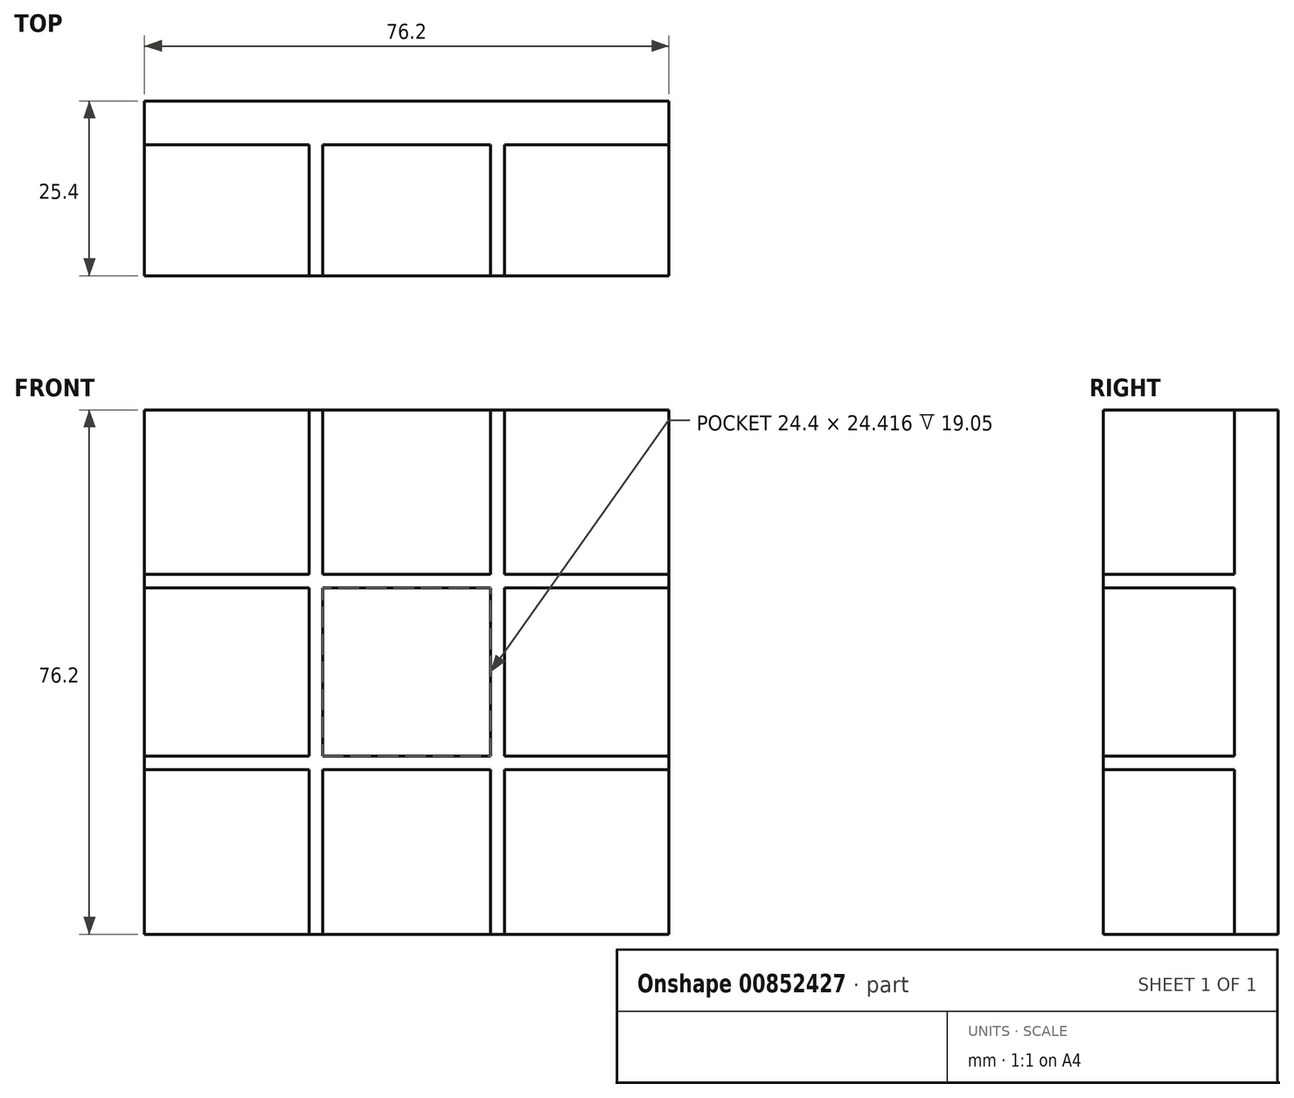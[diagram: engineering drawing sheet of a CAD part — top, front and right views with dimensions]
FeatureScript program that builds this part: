
annotation { "Feature Type Name" : "Feature", "Feature Type Description" : "" }
export const myFeature = defineFeature(function(context is Context, id is Id, definition is map)
    precondition{}
    {
        {
            var Q0;
            Q0=qCreatedBy(makeId("Front.planeOp"),FACE);
            var sketch = newSketch(context, id + "F0", { "sketchPlane" : qUnion([Q0])});
            skLineSegment(sketch, "E0.bottom", {"start": v(-38.2, 49.7) * mm, "end": v(38, 49.7) * mm});
            skLineSegment(sketch, "E0.top", {"start": v(-38.2, -26.5) * mm, "end": v(38, -26.5) * mm});
            skLineSegment(sketch, "E0.left", {"start": v(-38.2, 49.7) * mm, "end": v(-38.2, -26.5) * mm});
            skLineSegment(sketch, "E0.right", {"start": v(38, 49.7) * mm, "end": v(38, -26.5) * mm});
            skSolve(sketch);
        }
        {
            var Q0;
            Q0=makeQuery(id+"F0.imprint","IMPRINT",FACE,{"disambiguationData":[TD([[makeQuery(id+"F0.imprint","IMPRINT",EDGE,{"derivedFrom":sQuery(id+"F0.wireOp",EDGE,"E0.bottom")}),-1.0]])]});
            var sketch = newSketch(context, id + "F1", { "sketchPlane" : qUnion([Q0])});
            skLineSegment(sketch, "E1", {"start": v(-13.3, 49.7) * mm, "end": v(-13.3, -26.5) * mm});
            skLineSegment(sketch, "E2", {"start": v(13.1, 49.7) * mm, "end": v(13.1, -26.5) * mm});
            skLineSegment(sketch, "E3", {"start": v(-38.2, 24.8) * mm, "end": v(38, 24.8) * mm});
            skLineSegment(sketch, "E4", {"start": v(-38.2, -1.62) * mm, "end": v(38, -1.62) * mm});
            skSolve(sketch);
        }
        {
            var Q0;
            Q0=qCreatedBy(makeId("Front.planeOp"),FACE);
            var sketch = newSketch(context, id + "F2", { "sketchPlane" : qUnion([Q0])});
            skLineSegment(sketch, "E5", {"start": v(14.1, 49.7) * mm, "end": v(14.1, -26.5) * mm});
            skLineSegment(sketch, "E6", {"start": v(-14.3, 49.7) * mm, "end": v(-14.3, -26.5) * mm});
            skLineSegment(sketch, "E7", {"start": v(-38.2, 25.8) * mm, "end": v(38, 25.8) * mm});
            skLineSegment(sketch, "E8", {"start": v(-38.2, -2.62) * mm, "end": v(38, -2.62) * mm});
            skLineSegment(sketch, "E9", {"start": v(-38.2, -0.62) * mm, "end": v(38, -0.62) * mm});
            skLineSegment(sketch, "E10", {"start": v(-38.2, 23.8) * mm, "end": v(38, 23.8) * mm});
            skLineSegment(sketch, "E11", {"start": v(-12.3, 49.7) * mm, "end": v(-12.3, -26.5) * mm});
            skLineSegment(sketch, "E12", {"start": v(12.1, 49.7) * mm, "end": v(12.1, -26.5) * mm});
            skSolve(sketch);
        }
        {
            var Q0;
            Q0=makeQuery(id+"F0.imprint","IMPRINT",FACE,{"disambiguationData":[TD([[makeQuery(id+"F0.imprint","IMPRINT",EDGE,{"derivedFrom":sQuery(id+"F0.wireOp",EDGE,"E0.bottom")}),-1.0]])]});
            extrude(context, id + "F3", {"entities" : qUnion([Q0]), "depth" : 6.35 * mm, "offsetDistance" : 25.4 * mm});
        }
        {
            var Q0;
            Q0=sQuery(id+"F2.wireOp",EDGE,"E6");
            extrude(context, id + "F4", {"bodyType" : ToolBodyType.SURFACE, "surfaceEntities" : qUnion([Q0]), "depth" : 25.4 * mm, "offsetDistance" : 25.4 * mm});
        }
        {
            var Q0;
            Q0=sQuery(id+"F2.wireOp",EDGE,"E11");
            var Q1;
            Q1=sQuery(id+"F2.wireOp",EDGE,"E12");
            var Q2;
            Q2=sQuery(id+"F2.wireOp",EDGE,"E5");
            extrude(context, id + "F5", {"bodyType" : ToolBodyType.SURFACE, "surfaceEntities" : qUnion([Q0, Q1, Q2]), "depth" : 25.4 * mm, "offsetDistance" : 25.4 * mm});
        }
        {
            var Q0;
            Q0=sQuery(id+"F2.wireOp",EDGE,"E7");
            var Q1;
            Q1=sQuery(id+"F2.wireOp",EDGE,"E10");
            var Q2;
            Q2=sQuery(id+"F2.wireOp",EDGE,"E9");
            var Q3;
            Q3=sQuery(id+"F2.wireOp",EDGE,"E8");
            extrude(context, id + "F6", {"bodyType" : ToolBodyType.SURFACE, "surfaceEntities" : qUnion([Q0, Q1, Q2, Q3]), "depth" : 25.4 * mm, "offsetDistance" : 25.4 * mm});
        }
        {
            var Q0;
            Q0=makeQuery(id+"F6.opExtrude","SWEPT_FACE",FACE,{"disambiguationData":[OSD([sQuery(id+"F2.wireOp",EDGE,"E7")])]});
            extrude(context, id + "F7", {"entities" : qUnion([Q0]), "operationType" : NewBodyOperationType.ADD, "depth" : 2 * mm, "offsetDistance" : 25.4 * mm});
        }
        {
            var Q0;
            Q0=makeQuery(id+"F6.opExtrude","SWEPT_FACE",FACE,{"disambiguationData":[OSD([sQuery(id+"F2.wireOp",EDGE,"E9")])]});
            extrude(context, id + "F8", {"entities" : qUnion([Q0]), "operationType" : NewBodyOperationType.ADD, "depth" : 2 * mm, "offsetDistance" : 25.4 * mm});
        }
        {
            var Q0;
            Q0=makeQuery(id+"F5.opExtrude","SWEPT_FACE",FACE,{"disambiguationData":[OSD([sQuery(id+"F2.wireOp",EDGE,"E11")])]});
            var Q1;
            Q1=makeQuery(id+"F5.opExtrude","SWEPT_FACE",FACE,{"disambiguationData":[OSD([sQuery(id+"F2.wireOp",EDGE,"E5")])]});
            extrude(context, id + "F9", {"entities" : qUnion([Q0, Q1]), "operationType" : NewBodyOperationType.ADD, "depth" : 2 * mm, "offsetDistance" : 25.4 * mm});
        }
    });
